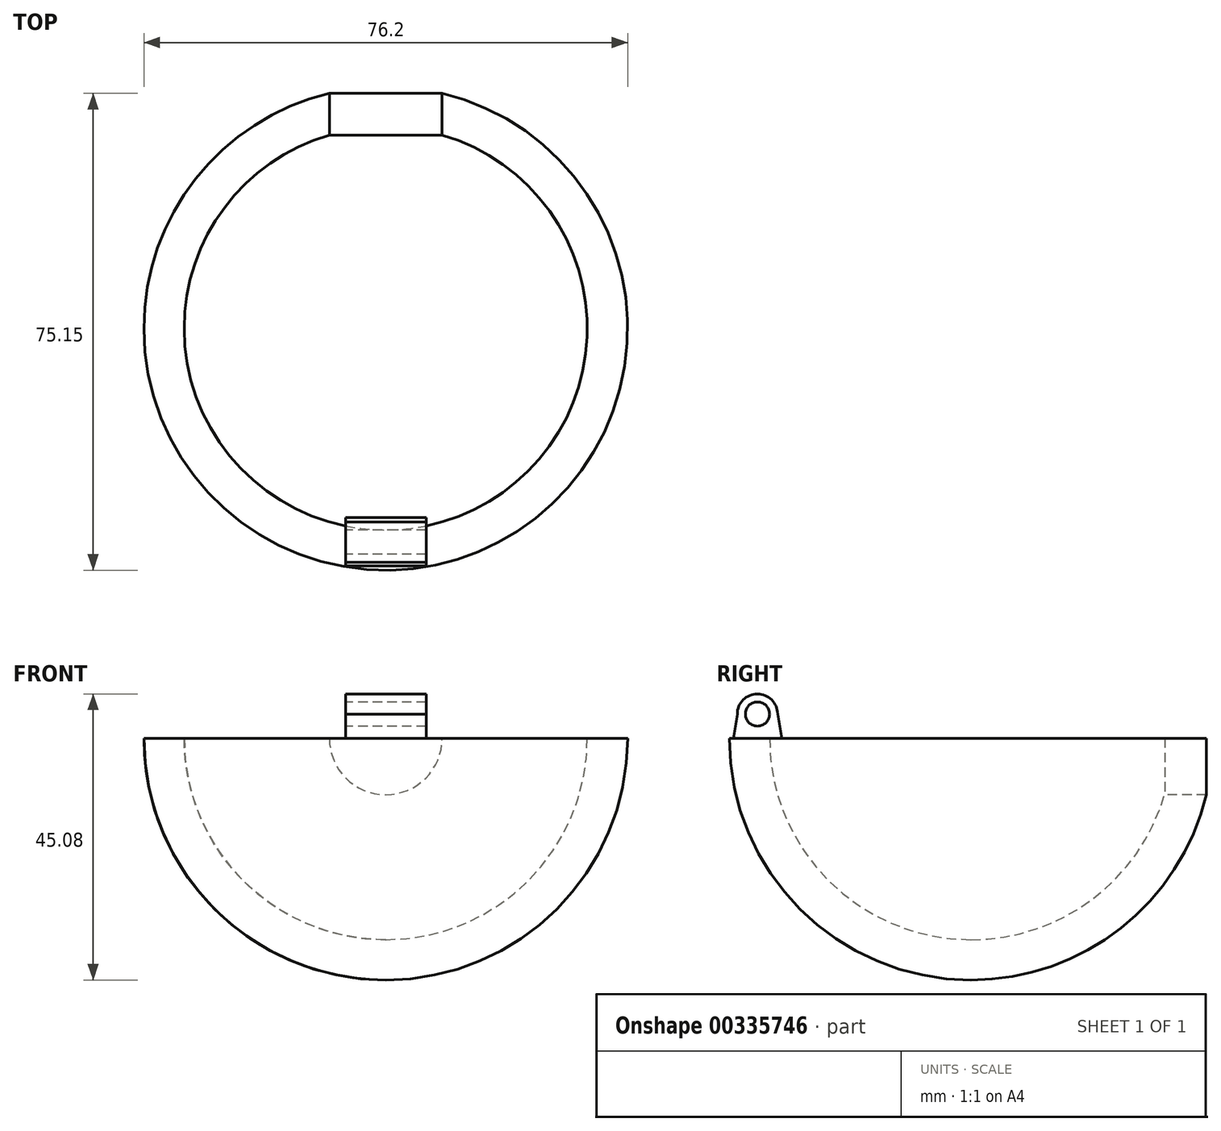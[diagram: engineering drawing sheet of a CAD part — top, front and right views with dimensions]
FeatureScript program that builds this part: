
annotation { "Feature Type Name" : "Feature", "Feature Type Description" : "" }
export const myFeature = defineFeature(function(context is Context, id is Id, definition is map)
    precondition{}
    {
        {
            var Q0;
            Q0=qCreatedBy(makeId("Front.planeOp"),FACE);
            var sketch = newSketch(context, id + "F0", { "sketchPlane" : qUnion([Q0])});
            skArc(sketch, "E0", {"start": v(-38.1, 0) * mm, "mid": v(-26.94, -26.94) * mm, "end": v(0, -38.1) * mm});
            skLineSegment(sketch, "E1", {"start": v(-38.1, 0) * mm, "end": v(-31.75, 0) * mm});
            skLineSegment(sketch, "E2", {"start": v(0, -31.75) * mm, "end": v(0, -38.1) * mm});
            skArc(sketch, "E3.0", {"start": v(-31.75, 0) * mm, "mid": v(-22.45, -22.45) * mm, "end": v(0, -31.75) * mm});
            skSolve(sketch);
        }
        {
            var Q0;
            Q0=makeQuery(id+"F0.imprint","IMPRINT",FACE,{"disambiguationData":[TD([[makeQuery(id+"F0.imprint","IMPRINT",EDGE,{"derivedFrom":sQuery(id+"F0.wireOp",EDGE,"E0")}),1.0]])]});
            var Q1;
            Q1=sQuery(id+"F0.wireOp",EDGE,"E2");
            revolve(context, id + "F1", {"entities" : qUnion([Q0]), "axis" : qUnion([Q1]), "revolveType" : RevolveType.FULL});
        }
        {
            var Q0;
            Q0=qCreatedBy(makeId("Front.planeOp"),FACE);
            var sketch = newSketch(context, id + "F2", { "sketchPlane" : qUnion([Q0])});
            skCircle(sketch, "E4", {"center": v(0, 0) * mm, "radius": 8.9 * mm});
            skSolve(sketch);
        }
        {
            var Q0;
            Q0=makeQuery(id+"F2.imprint","IMPRINT",FACE,{"disambiguationData":[TD([[makeQuery(id+"F2.imprint","IMPRINT",EDGE,{"derivedFrom":sQuery(id+"F2.wireOp",EDGE,"E4")}),1.0]])]});
            extrude(context, id + "F3", {"entities" : qUnion([Q0]), "operationType" : NewBodyOperationType.REMOVE, "endBound" : BoundingType.THROUGH_ALL, "oppositeDirection" : true, "depth" : 25.4 * mm});
        }
        {
            var Q0;
            Q0=qCreatedBy(makeId("Right.planeOp"),FACE);
            var sketch = newSketch(context, id + "F4", { "sketchPlane" : qUnion([Q0])});
            skCircle(sketch, "E5", {"center": v(-33.65, 3.81) * mm, "radius": 1.9 * mm});
            skLineSegment(sketch, "E6.0.0", {"start": v(37.05, 0) * mm, "end": v(-38.1, 0) * mm});
            skLineSegment(sketch, "E6.0.1", {"start": v(37.05, 0) * mm, "end": v(30.48, 0) * mm});
            skLineSegment(sketch, "E6.0.2", {"start": v(30.48, 0) * mm, "end": v(-31.75, 0) * mm});
            skLineSegment(sketch, "E6.0.3", {"start": v(30.48, 0) * mm, "end": v(37.05, 0) * mm});
            skArc(sketch, "E7.0", {"start": v(-30.48, 3.82) * mm, "mid": v(-33.66, 6.98) * mm, "end": v(-36.83, 3.8) * mm});
            skLineSegment(sketch, "E8", {"start": v(-36.83, 3.8) * mm, "end": v(-37.42, 0) * mm});
            skLineSegment(sketch, "E9", {"start": v(-37.42, 0) * mm, "end": v(-29.82, 0) * mm});
            skLineSegment(sketch, "E10", {"start": v(-29.82, 0) * mm, "end": v(-30.48, 3.82) * mm});
            skSolve(sketch);
        }
        {
            var Q0;
            Q0=makeQuery(id+"F4.imprint","IMPRINT",FACE,{"disambiguationData":[TD([[makeQuery(id+"F4.imprint","IMPRINT",EDGE,{"derivedFrom":sQuery(id+"F4.wireOp",EDGE,"E5")}),-1.0]])]});
            extrude(context, id + "F5", {"entities" : qUnion([Q0]), "operationType" : NewBodyOperationType.ADD, "endBound" : BoundingType.SYMMETRIC, "depth" : 12.7 * mm});
        }
    });
